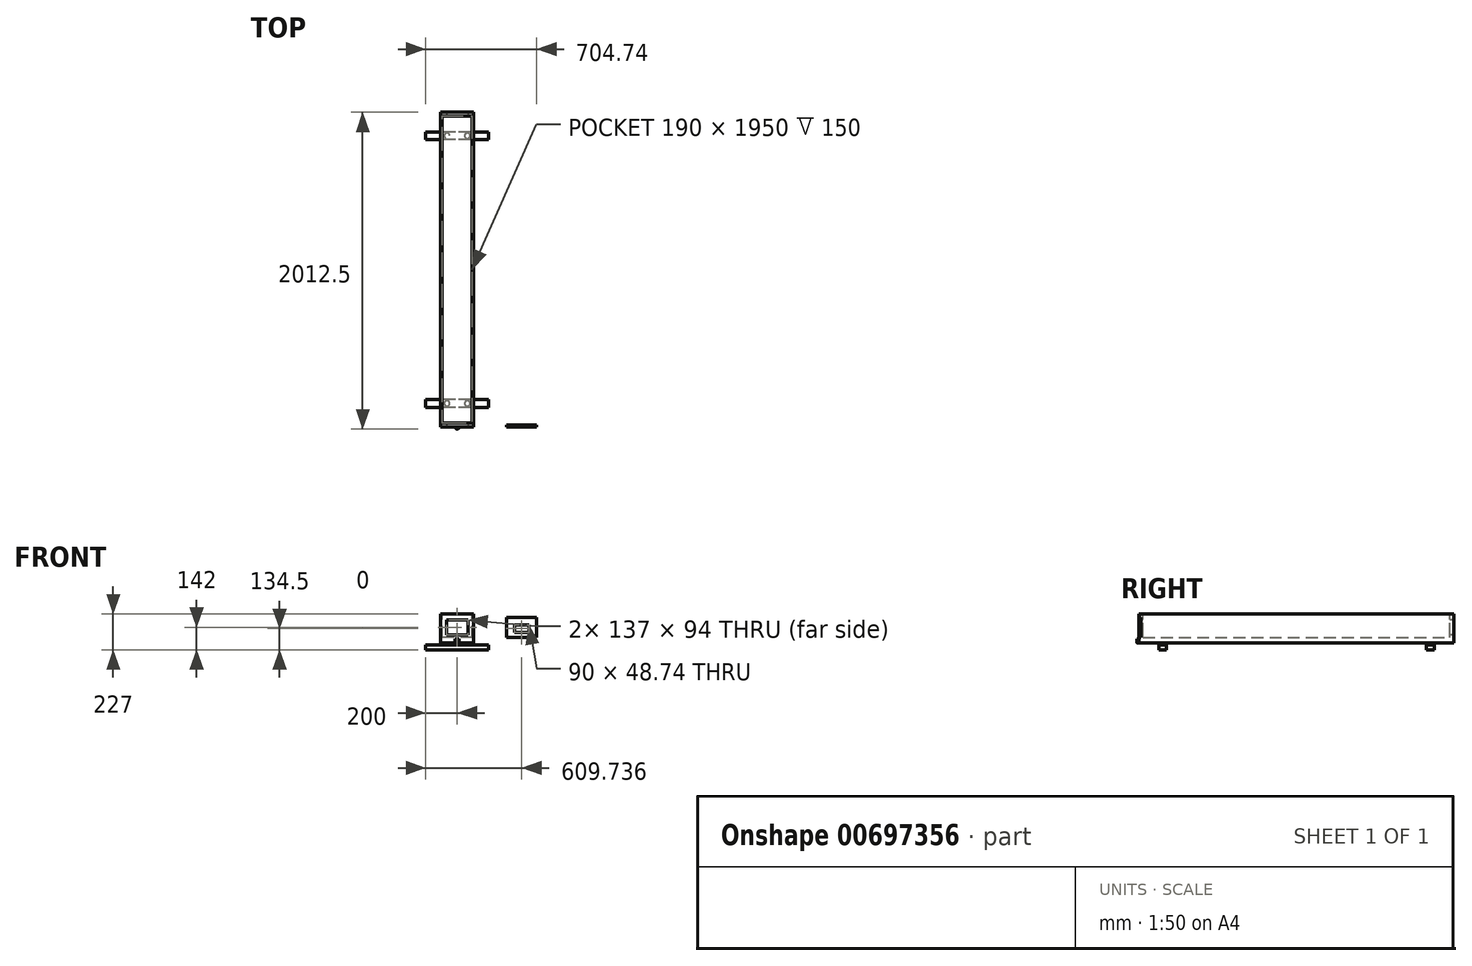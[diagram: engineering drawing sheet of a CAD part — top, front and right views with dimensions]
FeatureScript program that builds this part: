
annotation { "Feature Type Name" : "Feature", "Feature Type Description" : "" }
export const myFeature = defineFeature(function(context is Context, id is Id, definition is map)
    precondition{}
    {
        {
            var Q0;
            Q0=qCreatedBy(makeId("Front.planeOp"),FACE);
            var sketch = newSketch(context, id + "F0", { "sketchPlane" : qUnion([Q0])});
            skLineSegment(sketch, "E0.bottom", {"start": v(105, -92.5) * mm, "end": v(-105, -92.5) * mm});
            skLineSegment(sketch, "E0.top", {"start": v(105, 92.5) * mm, "end": v(-105, 92.5) * mm});
            skLineSegment(sketch, "E0.left", {"start": v(105, -92.5) * mm, "end": v(105, 92.5) * mm});
            skLineSegment(sketch, "E0.right", {"start": v(-105, -92.5) * mm, "end": v(-105, 92.5) * mm});
            skPoint(sketch, "E0.middle", {"position": v(0, 0) * mm});
            skSolve(sketch);
        }
        {
            var Q0;
            Q0 = qSketchRegion(id + "F0", true);
            extrude(context, id + "F1", {"entities" : qUnion([Q0]), "oppositeDirection" : true, "depth" : 2000 * mm, "offsetDistance" : 25 * mm});
        }
        {
            var Q0;
            Q0=makeQuery(id+"F1.opExtrude","CAP_FACE",FACE,{"disambiguationData":[OSD([sQuery(id+"F0.wireOp",EDGE,"E0.bottom"),sQuery(id+"F0.wireOp",EDGE,"E0.top"),sQuery(id+"F0.wireOp",EDGE,"E0.left"),sQuery(id+"F0.wireOp",EDGE,"E0.right")])],"isStart":true});
            var sketch = newSketch(context, id + "F2", { "sketchPlane" : qUnion([Q0])});
            skLineSegment(sketch, "E1", {"start": v(-68.5, 54.5) * mm, "end": v(68.5, 54.5) * mm});
            skLineSegment(sketch, "E2", {"start": v(68.5, 54.5) * mm, "end": v(68.5, -39.5) * mm});
            skLineSegment(sketch, "E3", {"start": v(68.5, -39.5) * mm, "end": v(-68.5, -39.5) * mm});
            skLineSegment(sketch, "E4", {"start": v(-68.5, -39.5) * mm, "end": v(-68.5, 54.5) * mm});
            skSolve(sketch);
        }
        {
            var Q0;
            Q0=makeQuery(id+"F2.imprint","IMPRINT",FACE,{"disambiguationData":[TD([[makeQuery(id+"F2.imprint","IMPRINT",EDGE,{"derivedFrom":sQuery(id+"F2.wireOp",EDGE,"E1")}),-1.0]])]});
            extrude(context, id + "F3", {"entities" : qUnion([Q0]), "operationType" : NewBodyOperationType.ADD, "oppositeDirection" : true, "depth" : 2100 * mm, "offsetDistance" : 25 * mm});
        }
        {
            var Q0;
            Q0=makeQuery(id+"F2.imprint","IMPRINT",FACE,{"disambiguationData":[TD([[makeQuery(id+"F2.imprint","IMPRINT",EDGE,{"derivedFrom":sQuery(id+"F2.wireOp",EDGE,"E1")}),-1.0]])]});
            extrude(context, id + "F4", {"entities" : qUnion([Q0]), "operationType" : NewBodyOperationType.REMOVE, "oppositeDirection" : true, "depth" : 2100 * mm, "offsetDistance" : 25 * mm});
        }
        {
            var Q0;
            Q0=makeQuery(id+"F1.opExtrude","SWEPT_FACE",FACE,{"disambiguationData":[OSD([sQuery(id+"F0.wireOp",EDGE,"E0.top")])]});
            var sketch = newSketch(context, id + "F5", { "sketchPlane" : qUnion([Q0])});
            skLineSegment(sketch, "E5.bottom", {"start": v(95, 25) * mm, "end": v(-95, 25) * mm});
            skLineSegment(sketch, "E5.top", {"start": v(95, 1975) * mm, "end": v(-95, 1975) * mm});
            skLineSegment(sketch, "E5.left", {"start": v(95, 25) * mm, "end": v(95, 1975) * mm});
            skLineSegment(sketch, "E5.right", {"start": v(-95, 25) * mm, "end": v(-95, 1975) * mm});
            skPoint(sketch, "E5.middle", {"position": v(0, 1000) * mm});
            skPoint(sketch, "E5.middle.positionSnap0", {"position": v(105, 1000) * mm});
            skPoint(sketch, "E5.centerSnap0", {"position": v(105, 1000) * mm});
            skSolve(sketch);
        }
        {
            var Q0;
            Q0=makeQuery(id+"F5.imprint","IMPRINT",FACE,{"disambiguationData":[TD([[makeQuery(id+"F5.imprint","IMPRINT",EDGE,{"derivedFrom":sQuery(id+"F5.wireOp",EDGE,"E5.bottom")}),-1.0]])]});
            extrude(context, id + "F6", {"entities" : qUnion([Q0]), "operationType" : NewBodyOperationType.REMOVE, "oppositeDirection" : true, "depth" : 150 * mm, "offsetDistance" : 25 * mm});
        }
        {
            var Q0;
            Q0=makeQuery(id+"F1.opExtrude","SWEPT_FACE",FACE,{"disambiguationData":[OSD([sQuery(id+"F0.wireOp",EDGE,"E0.bottom")])]});
            var sketch = newSketch(context, id + "F7", { "sketchPlane" : qUnion([Q0])});
            skCircle(sketch, "E6", {"center": v(0, 0) * mm, "radius": 12.5 * mm});
            skSolve(sketch);
        }
        {
            var Q0;
            {var subQ0=sQuery(id+"F7.wireOp",EDGE,"E6");var subQ1=makeQuery(id+"F1.opExtrude","CAP_EDGE",EDGE,{"disambiguationData":[OSD([sQuery(id+"F0.wireOp",EDGE,"E0.bottom")])],"isStart":true});var subQ2=makeQuery(id+"F7.imprint","INTERSECT",VERTEX,{"disambiguationData":[OD(0.0)],"derivedFrom":[subQ1,subQ0]});Q0=makeQuery(id+"F7.imprint","IMPRINT",FACE,{"disambiguationData":[TD([[makeQuery(id+"F7.imprint","IMPRINT",EDGE,{"disambiguationData":[TD([[subQ2,-1.0]])],"derivedFrom":subQ0}),1.0]])]});}
            extrude(context, id + "F8", {"entities" : qUnion([Q0]), "oppositeDirection" : true, "depth" : 25 * mm, "offsetDistance" : 25 * mm});
        }
        {
            var Q0;
            Q0=makeQuery(id+"F1.opExtrude","SWEPT_FACE",FACE,{"disambiguationData":[OSD([sQuery(id+"F0.wireOp",EDGE,"E0.bottom")])]});
            var sketch = newSketch(context, id + "F9", { "sketchPlane" : qUnion([Q0])});
            skCircle(sketch, "E7", {"center": v(-65, -1850) * mm, "radius": 17.5 * mm});
            skCircle(sketch, "E8", {"center": v(65, -1850) * mm, "radius": 17.5 * mm});
            skCircle(sketch, "E9", {"center": v(-65, -150) * mm, "radius": 17.5 * mm});
            skCircle(sketch, "E10", {"center": v(65, -150) * mm, "radius": 17.5 * mm});
            skSolve(sketch);
        }
        {
            var Q0;
            Q0=makeQuery(id+"F9.imprint","IMPRINT",FACE,{"disambiguationData":[TD([[makeQuery(id+"F9.imprint","IMPRINT",EDGE,{"derivedFrom":sQuery(id+"F9.wireOp",EDGE,"E8")}),1.0]])]});
            var Q1;
            Q1=makeQuery(id+"F9.imprint","IMPRINT",FACE,{"disambiguationData":[TD([[makeQuery(id+"F9.imprint","IMPRINT",EDGE,{"derivedFrom":sQuery(id+"F9.wireOp",EDGE,"E7")}),1.0]])]});
            var Q2;
            Q2=makeQuery(id+"F9.imprint","IMPRINT",FACE,{"disambiguationData":[TD([[makeQuery(id+"F9.imprint","IMPRINT",EDGE,{"derivedFrom":sQuery(id+"F9.wireOp",EDGE,"E10")}),1.0]])]});
            var Q3;
            Q3=makeQuery(id+"F9.imprint","IMPRINT",FACE,{"disambiguationData":[TD([[makeQuery(id+"F9.imprint","IMPRINT",EDGE,{"derivedFrom":sQuery(id+"F9.wireOp",EDGE,"E9")}),1.0]])]});
            extrude(context, id + "F10", {"entities" : qUnion([Q0, Q1, Q2, Q3]), "operationType" : NewBodyOperationType.ADD, "depth" : 12 * mm, "offsetDistance" : 25 * mm});
        }
        {
            var Q0;
            Q0=makeQuery(id+"F10.opExtrude","CAP_FACE",FACE,{"disambiguationData":[OSD([sQuery(id+"F9.wireOp",EDGE,"E9")])],"isStart":false});
            var sketch = newSketch(context, id + "F11", { "sketchPlane" : qUnion([Q0])});
            skLineSegment(sketch, "E11.bottom", {"start": v(200, -175) * mm, "end": v(-200, -175) * mm});
            skLineSegment(sketch, "E11.top", {"start": v(200, -125) * mm, "end": v(-200, -125) * mm});
            skLineSegment(sketch, "E11.left", {"start": v(200, -175) * mm, "end": v(200, -125) * mm});
            skLineSegment(sketch, "E11.right", {"start": v(-200, -175) * mm, "end": v(-200, -125) * mm});
            skPoint(sketch, "E11.middle", {"position": v(0, -150) * mm});
            skLineSegment(sketch, "E12.bottom", {"start": v(200, -1875) * mm, "end": v(-200, -1875) * mm});
            skLineSegment(sketch, "E12.top", {"start": v(200, -1825) * mm, "end": v(-200, -1825) * mm});
            skLineSegment(sketch, "E12.left", {"start": v(200, -1875) * mm, "end": v(200, -1825) * mm});
            skLineSegment(sketch, "E12.right", {"start": v(-200, -1875) * mm, "end": v(-200, -1825) * mm});
            skPoint(sketch, "E12.middle", {"position": v(0, -1850) * mm});
            skSolve(sketch);
        }
        {
            var Q0;
            Q0=makeQuery(id+"F11.imprint","IMPRINT",FACE,{"disambiguationData":[TD([[makeQuery(id+"F11.imprint","IMPRINT",EDGE,{"derivedFrom":sQuery(id+"F11.wireOp",EDGE,"E12.bottom")}),-1.0]])]});
            var Q1;
            Q1=makeQuery(id+"F11.imprint","IMPRINT",FACE,{"disambiguationData":[TD([[makeQuery(id+"F11.imprint","IMPRINT",EDGE,{"derivedFrom":sQuery(id+"F11.wireOp",EDGE,"E11.bottom")}),-1.0]])]});
            var Q2;
            Q2=makeQuery(id+"F11.imprint","IMPRINT",FACE,{"disambiguationData":[TD([[makeQuery(id+"F11.imprint","IMPRINT",EDGE,{"derivedFrom":makeQuery(id+"F10.opExtrude","CAP_EDGE",EDGE,{"disambiguationData":[OSD([sQuery(id+"F9.wireOp",EDGE,"E9")])],"isStart":false})}),1.0]])]});
            extrude(context, id + "F12", {"entities" : qUnion([Q0, Q1, Q2]), "depth" : 30 * mm, "offsetDistance" : 25 * mm});
        }
        {
            var Q0;
            Q0=makeQuery(id+"F1.opExtrude","CAP_FACE",FACE,{"disambiguationData":[OSD([sQuery(id+"F0.wireOp",EDGE,"E0.bottom"),sQuery(id+"F0.wireOp",EDGE,"E0.top"),sQuery(id+"F0.wireOp",EDGE,"E0.left"),sQuery(id+"F0.wireOp",EDGE,"E0.right")])],"isStart":true});
            var sketch = newSketch(context, id + "F13", { "sketchPlane" : qUnion([Q0])});
            skLineSegment(sketch, "E13.bottom", {"start": v(45, -24.37) * mm, "end": v(-45, -24.37) * mm});
            skLineSegment(sketch, "E13.top", {"start": v(45, 24.37) * mm, "end": v(-45, 24.37) * mm});
            skLineSegment(sketch, "E13.left", {"start": v(45, -24.37) * mm, "end": v(45, 24.37) * mm});
            skLineSegment(sketch, "E13.right", {"start": v(-45, -24.37) * mm, "end": v(-45, 24.37) * mm});
            skPoint(sketch, "E13.middle", {"position": v(0, 0) * mm});
            skLineSegment(sketch, "E14.bottom", {"start": v(504.74, -57.5) * mm, "end": v(314.74, -57.5) * mm});
            skLineSegment(sketch, "E14.top", {"start": v(504.74, 70.5) * mm, "end": v(314.74, 70.5) * mm});
            skLineSegment(sketch, "E14.left", {"start": v(504.74, -57.5) * mm, "end": v(504.74, 70.5) * mm});
            skLineSegment(sketch, "E14.right", {"start": v(314.74, -57.5) * mm, "end": v(314.74, 70.5) * mm});
            skPoint(sketch, "E14.middle", {"position": v(409.74, 0) * mm});
            skLineSegment(sketch, "E15.bottom", {"start": v(454.74, -24.37) * mm, "end": v(364.74, -24.37) * mm});
            skLineSegment(sketch, "E15.top", {"start": v(454.74, 24.37) * mm, "end": v(364.74, 24.37) * mm});
            skLineSegment(sketch, "E15.left", {"start": v(454.74, -24.37) * mm, "end": v(454.74, 24.37) * mm});
            skLineSegment(sketch, "E15.right", {"start": v(364.74, -24.37) * mm, "end": v(364.74, 24.37) * mm});
            skSolve(sketch);
        }
        {
            var Q0;
            Q0=makeQuery(id+"F13.imprint","IMPRINT",FACE,{"disambiguationData":[TD([[makeQuery(id+"F13.imprint","IMPRINT",EDGE,{"derivedFrom":sQuery(id+"F13.wireOp",EDGE,"E14.bottom")}),-1.0]])]});
            extrude(context, id + "F14", {"entities" : qUnion([Q0]), "oppositeDirection" : true, "depth" : 12 * mm, "offsetDistance" : 25 * mm});
        }
    });
